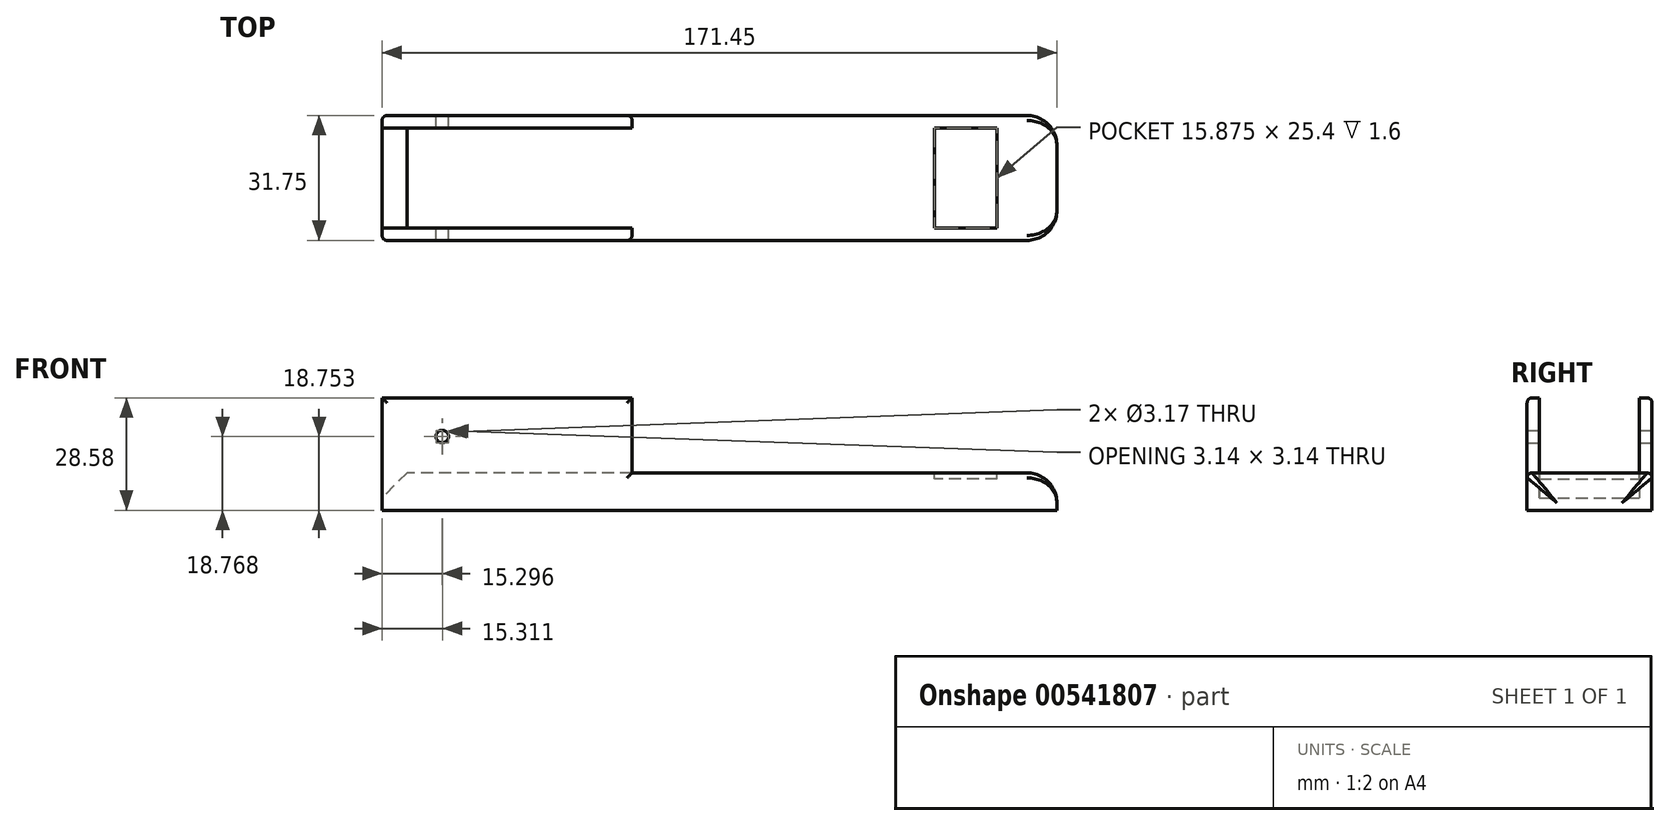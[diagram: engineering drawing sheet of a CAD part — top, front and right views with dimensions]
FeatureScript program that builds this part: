
annotation { "Feature Type Name" : "Feature", "Feature Type Description" : "" }
export const myFeature = defineFeature(function(context is Context, id is Id, definition is map)
    precondition{}
    {
        {
            var Q0;
            Q0=qCreatedBy(makeId("Top.planeOp"),FACE);
            var sketch = newSketch(context, id + "F0", { "sketchPlane" : qUnion([Q0])});
            skLineSegment(sketch, "E0", {"start": v(-51.83, 39.3) * mm, "end": v(119.62, 39.3) * mm});
            skLineSegment(sketch, "E1.0", {"start": v(-51.83, 7.55) * mm, "end": v(119.62, 7.55) * mm});
            skLineSegment(sketch, "E2", {"start": v(-51.83, 39.3) * mm, "end": v(-51.83, 7.55) * mm});
            skLineSegment(sketch, "E3", {"start": v(119.62, 39.3) * mm, "end": v(119.62, 7.55) * mm});
            skSolve(sketch);
        }
        {
            var Q0;
            Q0 = qSketchRegion(id + "F0", true);
            extrude(context, id + "F1", {"entities" : qUnion([Q0]), "oppositeDirection" : true, "depth" : 9.52 * mm, "offsetDistance" : 25.4 * mm});
        }
        {
            var Q0;
            Q0=qCreatedBy(makeId("Top.planeOp"),FACE);
            var sketch = newSketch(context, id + "F2", { "sketchPlane" : qUnion([Q0])});
            skLineSegment(sketch, "E4", {"start": v(11.67, 39.3) * mm, "end": v(-51.83, 39.3) * mm});
            skLineSegment(sketch, "E5", {"start": v(-51.83, 7.55) * mm, "end": v(11.67, 7.55) * mm});
            skLineSegment(sketch, "E6", {"start": v(11.67, 36.13) * mm, "end": v(11.67, 39.3) * mm});
            skLineSegment(sketch, "E7", {"start": v(11.67, 10.73) * mm, "end": v(11.67, 7.55) * mm});
            skLineSegment(sketch, "E8", {"start": v(11.67, 10.73) * mm, "end": v(-51.83, 10.73) * mm});
            skLineSegment(sketch, "E9", {"start": v(-51.83, 7.55) * mm, "end": v(-51.83, 10.73) * mm});
            skLineSegment(sketch, "E10", {"start": v(11.67, 36.13) * mm, "end": v(-51.83, 36.13) * mm});
            skLineSegment(sketch, "E11", {"start": v(-51.83, 36.13) * mm, "end": v(-51.83, 39.3) * mm});
            skSolve(sketch);
        }
        {
            var Q0;
            Q0 = qSketchRegion(id + "F2", true);
            extrude(context, id + "F3", {"entities" : qUnion([Q0]), "operationType" : NewBodyOperationType.ADD, "depth" : 19.05 * mm, "offsetDistance" : 25.4 * mm});
        }
        {
            var Q0;
            Q0=makeQuery(id+"F1.opExtrude","CAP_EDGE",EDGE,{"disambiguationData":[OSD([sQuery(id+"F0.wireOp",EDGE,"E0")])],"isStart":true});
            var Q1;
            Q1=makeQuery(id+"F1.opExtrude","CAP_EDGE",EDGE,{"disambiguationData":[OSD([sQuery(id+"F0.wireOp",EDGE,"E1.0")])],"isStart":true});
            fillet(context, id + "F4", {"entities" : qUnion([Q0, Q1]), "radius" : 1.27 * mm, "tangentPropagation" : true, "allowEdgeOverflow" : false});
        }
        {
            var Q0;
            Q0=makeQuery(id+"F3.boolean.opBoolean","MERGE",FACE,{"derivedFrom":[makeQuery(id+"F1.opExtrude","SWEPT_FACE",FACE,{"disambiguationData":[OSD([sQuery(id+"F0.wireOp",EDGE,"E0")])]}),makeQuery(id+"F3.opExtrude","SWEPT_FACE",FACE,{"disambiguationData":[OSD([sQuery(id+"F2.wireOp",EDGE,"E4")])]})]});
            var sketch = newSketch(context, id + "F5", { "sketchPlane" : qUnion([Q0])});
            skCircle(sketch, "E12", {"center": v(36.53, 9.24) * mm, "radius": 1.59 * mm});
            skSolve(sketch);
        }
        {
            var Q0;
            Q0=sQuery(id+"F5.wireOp",VERTEX,"E12.center");
            var Q1;
            Q1=makeQuery(id+"F1.opExtrude","SWEPT_BODY",BODY,{"disambiguationData":[OSD([sQuery(id+"F0.wireOp",EDGE,"E0"),sQuery(id+"F0.wireOp",EDGE,"E1.0"),sQuery(id+"F0.wireOp",EDGE,"E2"),sQuery(id+"F0.wireOp",EDGE,"E3")])]});
            hole(context, id + "F6", {"style" : HoleStyle.SIMPLE, "endStyle" : HoleEndStyle.THROUGH, "holeDiameter" : 3.17 * mm, "isTappedThrough" : true, "tappedDepth" : 12.7 * mm, "tapClearance" : 3, "locations" : qUnion([Q0]), "scope" : qUnion([Q1])});
        }
        {
            var Q0;
            Q0=makeQuery(id+"F1.opExtrude","CAP_FACE",FACE,{"disambiguationData":[OSD([sQuery(id+"F0.wireOp",EDGE,"E0"),sQuery(id+"F0.wireOp",EDGE,"E1.0"),sQuery(id+"F0.wireOp",EDGE,"E2"),sQuery(id+"F0.wireOp",EDGE,"E3")])],"isStart":true});
            var sketch = newSketch(context, id + "F7", { "sketchPlane" : qUnion([Q0])});
            skLineSegment(sketch, "E13.0", {"start": v(104.4, 10.73) * mm, "end": v(104.4, 36.13) * mm});
            skLineSegment(sketch, "E14.0", {"start": v(88.53, 10.73) * mm, "end": v(88.53, 36.13) * mm});
            skLineSegment(sketch, "E15.0", {"start": v(104.4, 36.13) * mm, "end": v(88.53, 36.13) * mm});
            skLineSegment(sketch, "E16.0", {"start": v(88.53, 10.73) * mm, "end": v(104.4, 10.73) * mm});
            skSolve(sketch);
        }
        {
            var Q0;
            Q0=makeQuery(id+"F7.imprint","IMPRINT",FACE,{"disambiguationData":[TD([[makeQuery(id+"F7.imprint","IMPRINT",EDGE,{"derivedFrom":sQuery(id+"F7.wireOp",EDGE,"E13.0")}),1.0]])]});
            extrude(context, id + "F8", {"entities" : qUnion([Q0]), "operationType" : NewBodyOperationType.REMOVE, "oppositeDirection" : true, "depth" : 1.6 * mm, "offsetDistance" : 25.4 * mm});
        }
        {
            var Q0;
            Q0=makeQuery(id+"F1.opExtrude","CAP_EDGE",EDGE,{"disambiguationData":[OSD([sQuery(id+"F0.wireOp",EDGE,"E2")])],"isStart":true});
            chamfer(context, id + "F9", {"entities" : qUnion([Q0]), "width" : 6.35 * mm, "tangentPropagation" : true});
        }
        {
            var Q0;
            Q0=makeQuery(id+"F3.opExtrude","SWEPT_EDGE",EDGE,{"disambiguationData":[OSD([sQuery(id+"F2.wireOp",EDGE,"E5"),sQuery(id+"F2.wireOp",EDGE,"E7")])]});
            var Q1;
            Q1=makeQuery(id+"F3.opExtrude","CAP_EDGE",EDGE,{"disambiguationData":[OSD([sQuery(id+"F2.wireOp",EDGE,"E5")])],"isStart":false});
            var Q2;
            Q2=makeQuery(id+"F3.boolean.opBoolean","MERGE",EDGE,{"derivedFrom":[makeQuery(id+"F1.opExtrude","SWEPT_EDGE",EDGE,{"disambiguationData":[OSD([sQuery(id+"F0.wireOp",EDGE,"E1.0"),sQuery(id+"F0.wireOp",EDGE,"E2")])]}),makeQuery(id+"F3.opExtrude","SWEPT_EDGE",EDGE,{"disambiguationData":[OSD([sQuery(id+"F2.wireOp",EDGE,"E5"),sQuery(id+"F2.wireOp",EDGE,"E9")])]})]});
            var Q3;
            Q3=makeQuery(id+"F3.opExtrude","SWEPT_EDGE",EDGE,{"disambiguationData":[OSD([sQuery(id+"F2.wireOp",EDGE,"E4"),sQuery(id+"F2.wireOp",EDGE,"E6")])]});
            var Q4;
            Q4=makeQuery(id+"F3.opExtrude","CAP_EDGE",EDGE,{"disambiguationData":[OSD([sQuery(id+"F2.wireOp",EDGE,"E4")])],"isStart":false});
            var Q5;
            Q5=makeQuery(id+"F3.boolean.opBoolean","MERGE",EDGE,{"derivedFrom":[makeQuery(id+"F1.opExtrude","SWEPT_EDGE",EDGE,{"disambiguationData":[OSD([sQuery(id+"F0.wireOp",EDGE,"E0"),sQuery(id+"F0.wireOp",EDGE,"E2")])]}),makeQuery(id+"F3.opExtrude","SWEPT_EDGE",EDGE,{"disambiguationData":[OSD([sQuery(id+"F2.wireOp",EDGE,"E4"),sQuery(id+"F2.wireOp",EDGE,"E11")])]})]});
            fillet(context, id + "F10", {"entities" : qUnion([Q0, Q1, Q2, Q3, Q4, Q5]), "radius" : 1.27 * mm, "tangentPropagation" : true, "allowEdgeOverflow" : false});
        }
        {
            var Q0;
            Q0=makeQuery(id+"F1.opExtrude","CAP_EDGE",EDGE,{"disambiguationData":[OSD([sQuery(id+"F0.wireOp",EDGE,"E3")])],"isStart":true});
            fillet(context, id + "F11", {"entities" : qUnion([Q0]), "radius" : 7.62 * mm, "tangentPropagation" : true, "allowEdgeOverflow" : false});
        }
    });
